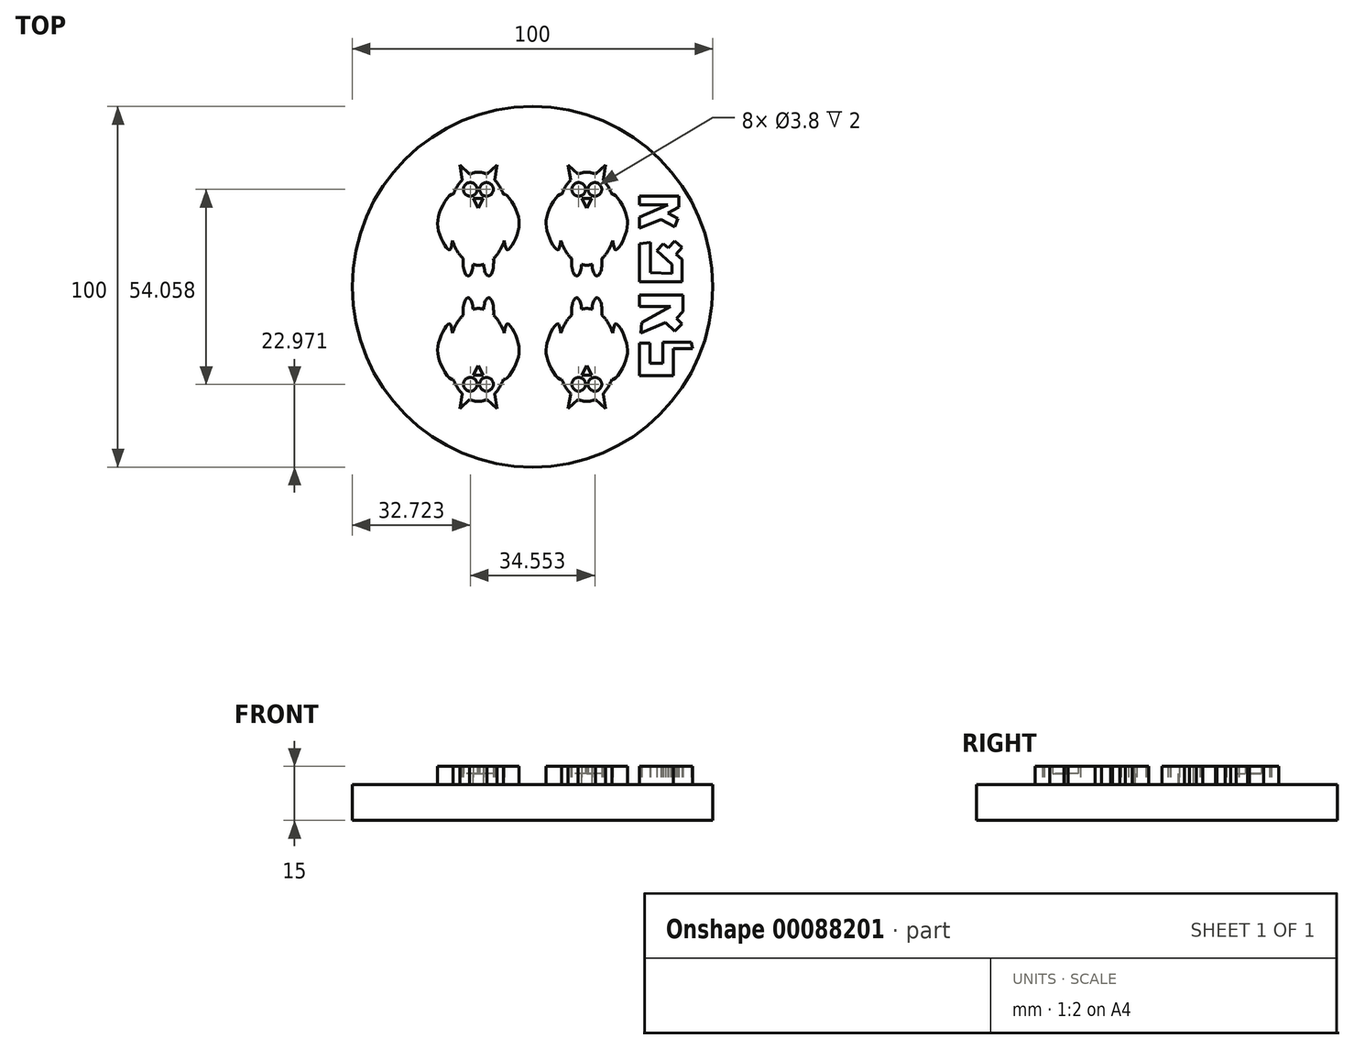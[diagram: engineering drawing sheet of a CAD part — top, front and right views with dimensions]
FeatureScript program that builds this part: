
annotation { "Feature Type Name" : "Feature", "Feature Type Description" : "" }
export const myFeature = defineFeature(function(context is Context, id is Id, definition is map)
    precondition{}
    {
        {
            var Q0;
            Q0=qCreatedBy(makeId("Top.planeOp"),FACE);
            var sketch = newSketch(context, id + "F0", { "sketchPlane" : qUnion([Q0])});
            skCircle(sketch, "E0", {"center": v(0, 0) * mm, "radius": 50 * mm});
            skSolve(sketch);
        }
        {
            var Q0;
            Q0 = qSketchRegion(id + "F0", true);
            extrude(context, id + "F1", {"entities" : qUnion([Q0]), "depth" : 10 * mm});
        }
        {
            var Q0;
            Q0=qCreatedBy(makeId("Top.planeOp"),FACE);
            var sketch = newSketch(context, id + "F2", { "sketchPlane" : qUnion([Q0])});
            skEllipse(sketch, "E1", {"center": v(-15.03, 18.9) * mm, "majorRadius": 12.9 * mm, "minorRadius": 8.17 * mm, "majorAxis": v(0, -1)});
            skPoint(sketch, "E2.3.internal.snap0", {"position": v(-23.2, 18.9) * mm});
            skFitSpline(sketch, "E2", {"points": [v(-22, 25.64) * mm, v(-25.43, 21.5) * mm, v(-25.86, 14.85) * mm, v(-23.2, 10.23) * mm, v(-22.24, 12.84) * mm, v(-22, 25.64) * mm]});
            skLineSegment(sketch, "E3", {"start": v(-15.03, 31.79) * mm, "end": v(-15.03, 6) * mm});
            skFitSpline(sketch, "E4.MirrorCS", {"points": [v(-8.07, 25.64) * mm, v(-4.63, 21.5) * mm, v(-4.2, 14.85) * mm, v(-6.86, 10.23) * mm, v(-7.82, 12.84) * mm, v(-8.07, 25.64) * mm]});
            skEllipse(sketch, "E5.MirrorC", {"center": v(15.03, 18.9) * mm, "majorRadius": 12.9 * mm, "minorRadius": 8.17 * mm, "majorAxis": v(0, -1)});
            skFitSpline(sketch, "E6.MirrorCS", {"points": [v(22, 25.64) * mm, v(25.43, 21.5) * mm, v(25.86, 14.85) * mm, v(23.2, 10.23) * mm, v(22.24, 12.84) * mm, v(22, 25.64) * mm]});
            skLineSegment(sketch, "E7.MirrorCS", {"start": v(15.03, 31.79) * mm, "end": v(15.03, 6) * mm});
            skFitSpline(sketch, "E8.MirrorCS", {"points": [v(8.07, 25.64) * mm, v(4.63, 21.5) * mm, v(4.2, 14.85) * mm, v(6.86, 10.23) * mm, v(7.82, 12.84) * mm, v(8.07, 25.64) * mm]});
            skPoint(sketch, "E9.MirrorP", {"position": v(23.2, 18.9) * mm});
            skPoint(sketch, "E10.MirrorP", {"position": v(-23.2, -18.9) * mm});
            skEllipse(sketch, "E11.MirrorC", {"center": v(-15.03, -18.9) * mm, "majorRadius": 12.9 * mm, "minorRadius": 8.17 * mm, "majorAxis": v(0, 1)});
            skFitSpline(sketch, "E12.MirrorCS", {"points": [v(-22, -25.64) * mm, v(-25.43, -21.5) * mm, v(-25.86, -14.85) * mm, v(-23.2, -10.23) * mm, v(-22.24, -12.84) * mm, v(-22, -25.64) * mm]});
            skLineSegment(sketch, "E13.MirrorCS", {"start": v(-15.03, -31.79) * mm, "end": v(-15.03, -6) * mm});
            skFitSpline(sketch, "E14.MirrorCS", {"points": [v(-8.07, -25.64) * mm, v(-4.63, -21.5) * mm, v(-4.2, -14.85) * mm, v(-6.86, -10.23) * mm, v(-7.82, -12.84) * mm, v(-8.07, -25.64) * mm]});
            skFitSpline(sketch, "E15.MirrorCS", {"points": [v(8.07, -25.64) * mm, v(4.63, -21.5) * mm, v(4.2, -14.85) * mm, v(6.86, -10.23) * mm, v(7.82, -12.84) * mm, v(8.07, -25.64) * mm]});
            skLineSegment(sketch, "E16.MirrorCS", {"start": v(15.03, -31.79) * mm, "end": v(15.03, -6) * mm});
            skEllipse(sketch, "E17.MirrorC", {"center": v(15.03, -18.9) * mm, "majorRadius": 12.9 * mm, "minorRadius": 8.17 * mm, "majorAxis": v(0, 1)});
            skPoint(sketch, "E18.MirrorP", {"position": v(23.2, -18.9) * mm});
            skFitSpline(sketch, "E19.MirrorCS", {"points": [v(22, -25.64) * mm, v(25.43, -21.5) * mm, v(25.86, -14.85) * mm, v(23.2, -10.23) * mm, v(22.24, -12.84) * mm, v(22, -25.64) * mm]});
            skSolve(sketch);
        }
        {
            var Q0;
            Q0=qCreatedBy(makeId("Top.planeOp"),FACE);
            var sketch = newSketch(context, id + "F3", { "sketchPlane" : qUnion([Q0])});
            skLineSegment(sketch, "E20", {"start": v(-19.47, 29.2) * mm, "end": v(-20.18, 33.8) * mm});
            skLineSegment(sketch, "E21", {"start": v(-20.18, 33.8) * mm, "end": v(-17.02, 30.84) * mm});
            skLineSegment(sketch, "E22", {"start": v(-17.02, 30.84) * mm, "end": v(-19.47, 29.2) * mm});
            skLineSegment(sketch, "E23.MirrorCS", {"start": v(-10.6, 29.2) * mm, "end": v(-9.88, 33.8) * mm});
            skLineSegment(sketch, "E24.MirrorCS", {"start": v(-13.04, 30.84) * mm, "end": v(-10.6, 29.2) * mm});
            skLineSegment(sketch, "E25.MirrorCS", {"start": v(-9.88, 33.8) * mm, "end": v(-13.04, 30.84) * mm});
            skLineSegment(sketch, "E26.MirrorCS", {"start": v(13.04, 30.84) * mm, "end": v(10.6, 29.2) * mm});
            skLineSegment(sketch, "E27.MirrorCS", {"start": v(17.02, 30.84) * mm, "end": v(19.47, 29.2) * mm});
            skLineSegment(sketch, "E28.MirrorCS", {"start": v(9.88, 33.8) * mm, "end": v(13.04, 30.84) * mm});
            skLineSegment(sketch, "E29.MirrorCS", {"start": v(10.6, 29.2) * mm, "end": v(9.88, 33.8) * mm});
            skLineSegment(sketch, "E30.MirrorCS", {"start": v(20.18, 33.8) * mm, "end": v(17.02, 30.84) * mm});
            skLineSegment(sketch, "E31.MirrorCS", {"start": v(19.47, 29.2) * mm, "end": v(20.18, 33.8) * mm});
            skLineSegment(sketch, "E32.MirrorCS", {"start": v(17.02, -30.84) * mm, "end": v(19.47, -29.2) * mm});
            skLineSegment(sketch, "E33.MirrorCS", {"start": v(-17.02, -30.84) * mm, "end": v(-19.47, -29.2) * mm});
            skLineSegment(sketch, "E34.MirrorCS", {"start": v(-13.04, -30.84) * mm, "end": v(-10.6, -29.2) * mm});
            skLineSegment(sketch, "E35.MirrorCS", {"start": v(13.04, -30.84) * mm, "end": v(10.6, -29.2) * mm});
            skLineSegment(sketch, "E36.MirrorCS", {"start": v(19.47, -29.2) * mm, "end": v(20.18, -33.8) * mm});
            skLineSegment(sketch, "E37.MirrorCS", {"start": v(20.18, -33.8) * mm, "end": v(17.02, -30.84) * mm});
            skLineSegment(sketch, "E38.MirrorCS", {"start": v(10.6, -29.2) * mm, "end": v(9.88, -33.8) * mm});
            skLineSegment(sketch, "E39.MirrorCS", {"start": v(9.88, -33.8) * mm, "end": v(13.04, -30.84) * mm});
            skLineSegment(sketch, "E40.MirrorCS", {"start": v(-10.6, -29.2) * mm, "end": v(-9.88, -33.8) * mm});
            skLineSegment(sketch, "E41.MirrorCS", {"start": v(-9.88, -33.8) * mm, "end": v(-13.04, -30.84) * mm});
            skLineSegment(sketch, "E42.MirrorCS", {"start": v(-20.18, -33.8) * mm, "end": v(-17.02, -30.84) * mm});
            skLineSegment(sketch, "E43.MirrorCS", {"start": v(-19.47, -29.2) * mm, "end": v(-20.18, -33.8) * mm});
            skEllipse(sketch, "E44", {"center": v(-17.87, 6.85) * mm, "majorRadius": 3.82 * mm, "minorRadius": 1.4 * mm, "majorAxis": v(0, -1)});
            skEllipse(sketch, "E45.MirrorC", {"center": v(-12.2, 6.85) * mm, "majorRadius": 3.82 * mm, "minorRadius": 1.4 * mm, "majorAxis": v(0, -1)});
            skEllipse(sketch, "E46.MirrorC", {"center": v(12.2, 6.85) * mm, "majorRadius": 3.82 * mm, "minorRadius": 1.4 * mm, "majorAxis": v(0, -1)});
            skEllipse(sketch, "E47.MirrorC", {"center": v(17.87, 6.85) * mm, "majorRadius": 3.82 * mm, "minorRadius": 1.4 * mm, "majorAxis": v(0, -1)});
            skEllipse(sketch, "E48.MirrorC", {"center": v(12.2, -6.85) * mm, "majorRadius": 3.82 * mm, "minorRadius": 1.4 * mm, "majorAxis": v(0, 1)});
            skEllipse(sketch, "E49.MirrorC", {"center": v(-17.87, -6.85) * mm, "majorRadius": 3.82 * mm, "minorRadius": 1.4 * mm, "majorAxis": v(0, 1)});
            skEllipse(sketch, "E50.MirrorC", {"center": v(-12.2, -6.85) * mm, "majorRadius": 3.82 * mm, "minorRadius": 1.4 * mm, "majorAxis": v(0, 1)});
            skEllipse(sketch, "E51.MirrorC", {"center": v(17.87, -6.85) * mm, "majorRadius": 3.82 * mm, "minorRadius": 1.4 * mm, "majorAxis": v(0, 1)});
            skSolve(sketch);
        }
        {
            var Q0;
            Q0 = qSketchRegion(id + "F2", true);
            extrude(context, id + "F4", {"entities" : qUnion([Q0]), "operationType" : NewBodyOperationType.ADD, "depth" : 15 * mm});
        }
        {
            var Q0;
            Q0 = qSketchRegion(id + "F3", true);
            extrude(context, id + "F5", {"entities" : qUnion([Q0]), "operationType" : NewBodyOperationType.ADD, "depth" : 15 * mm});
        }
        {
            var Q0;
            Q0=qCreatedBy(makeId("Top.planeOp"),FACE);
            cPlane(context, id + "F6", {"entities" : qUnion([Q0]), "cplaneType" : CPlaneType.OFFSET, "offset" : 13 * mm, "width" : 150 * mm, "height" : 150 * mm});
        }
        {
            var Q0;
            Q0=qCreatedBy(id+"F6.planeOp",FACE);
            var sketch = newSketch(context, id + "F7", { "sketchPlane" : qUnion([Q0])});
            skCircle(sketch, "E52", {"center": v(-17.28, 27.03) * mm, "radius": 1.9 * mm});
            skCircle(sketch, "E53.MirrorC", {"center": v(-12.79, 27.03) * mm, "radius": 1.9 * mm});
            skCircle(sketch, "E54.MirrorC", {"center": v(17.28, 27.03) * mm, "radius": 1.9 * mm});
            skCircle(sketch, "E55.MirrorC", {"center": v(12.79, 27.03) * mm, "radius": 1.9 * mm});
            skCircle(sketch, "E56.MirrorC", {"center": v(17.28, -27.03) * mm, "radius": 1.9 * mm});
            skCircle(sketch, "E57.MirrorC", {"center": v(-12.79, -27.03) * mm, "radius": 1.9 * mm});
            skCircle(sketch, "E58.MirrorC", {"center": v(12.79, -27.03) * mm, "radius": 1.9 * mm});
            skCircle(sketch, "E59.MirrorC", {"center": v(-17.28, -27.03) * mm, "radius": 1.9 * mm});
            skSolve(sketch);
        }
        {
            var Q0;
            Q0 = qSketchRegion(id + "F7", true);
            extrude(context, id + "F8", {"entities" : qUnion([Q0]), "operationType" : NewBodyOperationType.REMOVE, "depth" : 5 * mm});
        }
        {
            var Q0;
            Q0=qCreatedBy(id+"F6.planeOp",FACE);
            var sketch = newSketch(context, id + "F9", { "sketchPlane" : qUnion([Q0])});
            skLineSegment(sketch, "E60", {"start": v(-16.42, 24.53) * mm, "end": v(-14.93, 24.53) * mm});
            skLineSegment(sketch, "E61", {"start": v(-15.03, 21.82) * mm, "end": v(-16.42, 24.53) * mm});
            skLineSegment(sketch, "E62.MirrorCS", {"start": v(-15.03, 21.82) * mm, "end": v(-13.65, 24.53) * mm});
            skLineSegment(sketch, "E63.MirrorCS", {"start": v(-13.65, 24.53) * mm, "end": v(-15.13, 24.53) * mm});
            skPoint(sketch, "E64.orphan", {"position": v(-14.93, 21.62) * mm});
            skPoint(sketch, "E65.orphan", {"position": v(-15.13, 21.62) * mm});
            skLineSegment(sketch, "E66.MirrorCS", {"start": v(16.42, 24.53) * mm, "end": v(14.93, 24.53) * mm});
            skLineSegment(sketch, "E67.MirrorCS", {"start": v(13.65, 24.53) * mm, "end": v(15.13, 24.53) * mm});
            skLineSegment(sketch, "E68.MirrorCS", {"start": v(15.03, 21.82) * mm, "end": v(16.42, 24.53) * mm});
            skLineSegment(sketch, "E69.MirrorCS", {"start": v(15.03, 21.82) * mm, "end": v(13.65, 24.53) * mm});
            skPoint(sketch, "E70.MirrorP", {"position": v(15.13, 21.62) * mm});
            skPoint(sketch, "E71.MirrorP", {"position": v(14.93, 21.62) * mm});
            skLineSegment(sketch, "E72.MirrorCS", {"start": v(16.42, -24.53) * mm, "end": v(14.93, -24.53) * mm});
            skLineSegment(sketch, "E73.MirrorCS", {"start": v(13.65, -24.53) * mm, "end": v(15.13, -24.53) * mm});
            skLineSegment(sketch, "E74.MirrorCS", {"start": v(15.03, -21.82) * mm, "end": v(16.42, -24.53) * mm});
            skLineSegment(sketch, "E75.MirrorCS", {"start": v(15.03, -21.82) * mm, "end": v(13.65, -24.53) * mm});
            skLineSegment(sketch, "E76.MirrorCS", {"start": v(-15.03, -21.82) * mm, "end": v(-13.65, -24.53) * mm});
            skLineSegment(sketch, "E77.MirrorCS", {"start": v(-15.03, -21.82) * mm, "end": v(-16.42, -24.53) * mm});
            skLineSegment(sketch, "E78.MirrorCS", {"start": v(-16.42, -24.53) * mm, "end": v(-14.93, -24.53) * mm});
            skLineSegment(sketch, "E79.MirrorCS", {"start": v(-13.65, -24.53) * mm, "end": v(-15.13, -24.53) * mm});
            skPoint(sketch, "E80.MirrorP", {"position": v(14.93, -21.62) * mm});
            skPoint(sketch, "E81.MirrorP", {"position": v(-15.13, -21.62) * mm});
            skPoint(sketch, "E82.MirrorP", {"position": v(-14.93, -21.62) * mm});
            skPoint(sketch, "E83.MirrorP", {"position": v(15.13, -21.62) * mm});
            skSolve(sketch);
        }
        {
            var Q0;
            Q0 = qSketchRegion(id + "F9", true);
            extrude(context, id + "F10", {"entities" : qUnion([Q0]), "operationType" : NewBodyOperationType.REMOVE, "depth" : 5 * mm});
        }
        {
            var Q0;
            Q0=qCreatedBy(makeId("Top.planeOp"),FACE);
            var sketch = newSketch(context, id + "F11", { "sketchPlane" : qUnion([Q0])});
            skLineSegment(sketch, "E84", {"start": v(44.33, -17.18) * mm, "end": v(38.98, -17.18) * mm});
            skLineSegment(sketch, "E85", {"start": v(38.98, -17.18) * mm, "end": v(38.98, -24.63) * mm});
            skLineSegment(sketch, "E86", {"start": v(38.98, -24.63) * mm, "end": v(29.58, -24.63) * mm});
            skLineSegment(sketch, "E87", {"start": v(29.58, -24.63) * mm, "end": v(29.58, -15.55) * mm});
            skLineSegment(sketch, "E88", {"start": v(29.58, -15.55) * mm, "end": v(32.5, -15.55) * mm});
            skLineSegment(sketch, "E89", {"start": v(32.5, -15.55) * mm, "end": v(32.5, -21.23) * mm});
            skLineSegment(sketch, "E90", {"start": v(32.5, -21.23) * mm, "end": v(36.06, -21.23) * mm});
            skLineSegment(sketch, "E91", {"start": v(36.06, -21.23) * mm, "end": v(36.06, -15.4) * mm});
            skLineSegment(sketch, "E92", {"start": v(36.06, -15.4) * mm, "end": v(44, -15.4) * mm});
            skLineSegment(sketch, "E93", {"start": v(44, -15.4) * mm, "end": v(44.33, -17.18) * mm});
            skLineSegment(sketch, "E94", {"start": v(30.22, -9.88) * mm, "end": v(38.33, -5.5) * mm});
            skLineSegment(sketch, "E95", {"start": v(38.33, -5.5) * mm, "end": v(29.58, -5.5) * mm});
            skLineSegment(sketch, "E96", {"start": v(29.58, -5.5) * mm, "end": v(29.58, -2.26) * mm});
            skLineSegment(sketch, "E97", {"start": v(29.58, -2.26) * mm, "end": v(41.73, -2.26) * mm});
            skLineSegment(sketch, "E98", {"start": v(41.73, -2.26) * mm, "end": v(41.73, -6.8) * mm});
            skLineSegment(sketch, "E99", {"start": v(41.73, -6.8) * mm, "end": v(39.87, -8.78) * mm});
            skLineSegment(sketch, "E100", {"start": v(39.87, -8.78) * mm, "end": v(41.4, -10.23) * mm});
            skLineSegment(sketch, "E101", {"start": v(41.4, -10.23) * mm, "end": v(39.45, -12.31) * mm});
            skLineSegment(sketch, "E102", {"start": v(39.45, -12.31) * mm, "end": v(36.87, -9.88) * mm});
            skLineSegment(sketch, "E103", {"start": v(36.87, -9.88) * mm, "end": v(30.06, -12.8) * mm});
            skLineSegment(sketch, "E104", {"start": v(30.06, -12.8) * mm, "end": v(30.22, -9.88) * mm});
            skPoint(sketch, "E105.end.orphan", {"position": v(29.58, 3.74) * mm});
            skPoint(sketch, "E105.start.orphan", {"position": v(29.58, 1.47) * mm});
            skPoint(sketch, "E106.end.orphan", {"position": v(29.58, 9.4) * mm});
            skPoint(sketch, "E107.end.orphan", {"position": v(41.4, 1.47) * mm});
            skPoint(sketch, "E107.start.orphan", {"position": v(41.4, 4.87) * mm});
            skPoint(sketch, "E108.start.orphan", {"position": v(41.4, 12.49) * mm});
            skLineSegment(sketch, "E109", {"start": v(29.58, 12) * mm, "end": v(29.58, 1.47) * mm});
            skLineSegment(sketch, "E110", {"start": v(41.4, 1.47) * mm, "end": v(29.58, 1.47) * mm});
            skLineSegment(sketch, "E111", {"start": v(41.4, 1.47) * mm, "end": v(41.4, 7.63) * mm});
            skLineSegment(sketch, "E112", {"start": v(41.4, 7.63) * mm, "end": v(39.79, 9.09) * mm});
            skLineSegment(sketch, "E113", {"start": v(39.79, 9.09) * mm, "end": v(41.4, 10.89) * mm});
            skLineSegment(sketch, "E114", {"start": v(41.4, 10.89) * mm, "end": v(39.38, 12.7) * mm});
            skLineSegment(sketch, "E115", {"start": v(39.38, 12.7) * mm, "end": v(37.62, 10.75) * mm});
            skLineSegment(sketch, "E116", {"start": v(37.62, 10.75) * mm, "end": v(36.22, 12) * mm});
            skLineSegment(sketch, "E117", {"start": v(36.22, 12) * mm, "end": v(34.47, 10.06) * mm});
            skLineSegment(sketch, "E118", {"start": v(34.47, 10.06) * mm, "end": v(38.7, 6.25) * mm});
            skLineSegment(sketch, "E119", {"start": v(38.7, 6.25) * mm, "end": v(38.7, 3.74) * mm});
            skLineSegment(sketch, "E120", {"start": v(38.7, 3.74) * mm, "end": v(32.66, 3.9) * mm});
            skLineSegment(sketch, "E121", {"start": v(32.66, 3.9) * mm, "end": v(32.66, 12.33) * mm});
            skLineSegment(sketch, "E122", {"start": v(32.66, 12.33) * mm, "end": v(29.58, 12) * mm});
            skLineSegment(sketch, "E123", {"start": v(29.58, 16.22) * mm, "end": v(29.58, 19.3) * mm});
            skLineSegment(sketch, "E124", {"start": v(29.58, 19.3) * mm, "end": v(37.52, 22.7) * mm});
            skLineSegment(sketch, "E125", {"start": v(37.52, 22.7) * mm, "end": v(29.58, 22.7) * mm});
            skLineSegment(sketch, "E126", {"start": v(29.58, 22.7) * mm, "end": v(29.58, 25.13) * mm});
            skLineSegment(sketch, "E127", {"start": v(29.58, 25.13) * mm, "end": v(40.6, 25.13) * mm});
            skLineSegment(sketch, "E128", {"start": v(40.6, 25.13) * mm, "end": v(40.6, 22.05) * mm});
            skLineSegment(sketch, "E129", {"start": v(40.6, 22.05) * mm, "end": v(37.52, 20.43) * mm});
            skLineSegment(sketch, "E130", {"start": v(37.52, 20.43) * mm, "end": v(40.27, 18.97) * mm});
            skLineSegment(sketch, "E131", {"start": v(40.27, 18.97) * mm, "end": v(39.46, 16.7) * mm});
            skLineSegment(sketch, "E132", {"start": v(39.46, 16.7) * mm, "end": v(35.57, 18.65) * mm});
            skLineSegment(sketch, "E133", {"start": v(35.57, 18.65) * mm, "end": v(29.58, 16.22) * mm});
            skSolve(sketch);
        }
        {
            var Q0;
            Q0 = qSketchRegion(id + "F11", true);
            extrude(context, id + "F12", {"entities" : qUnion([Q0]), "operationType" : NewBodyOperationType.ADD, "depth" : 15 * mm});
        }
    });
